FCSTD DOCUMENT  (FreeCAD 1.0R39319 (Git))
Label: 00_assembly_basic_grate
License: All rights reserved
LicenseURL: http://en.wikipedia.org/wiki/All_rights_reserved
objects: App::Link×27, App::FeaturePython×14, Assembly::AssemblyLink×7, TechDraw::DrawProjGroupItem×6, TechDraw::DrawViewBalloon×5, TechDraw::DrawProjGroup×2, TechDraw::DrawSVGTemplate×1, Assembly::JointGroup×1, Assembly::AssemblyObject×1, TechDraw::DrawViewAnnotation×1, TechDraw::DrawPage×1
EXTERNAL_REF file=01_assembly_frame.FCStd obj=Assembly
EXTERNAL_REF file=01_assembly_frame.FCStd obj=Body
EXTERNAL_REF file=01_assembly_frame.FCStd obj=Body001
EXTERNAL_REF file=01_assembly_frame.FCStd obj=Body002
EXTERNAL_REF file=01_assembly_frame.FCStd obj=Body003
EXTERNAL_REF file=01_assembly_frame.FCStd obj=Body004
EXTERNAL_REF file=01_assembly_frame.FCStd obj=Body005
EXTERNAL_REF file=01_assembly_frame.FCStd obj=Body006
EXTERNAL_REF file=10_assembly_lamella_no_knob.FCStd obj=Assembly
EXTERNAL_REF file=10_assembly_lamella_no_knob.FCStd obj=Body
EXTERNAL_REF file=10_assembly_lamella_no_knob.FCStd obj=Body001
EXTERNAL_REF file=10_assembly_lamella_no_knob.FCStd obj=Body002
EXTERNAL_REF file=11_assembly_lamella_knob.FCStd obj=Assembly
EXTERNAL_REF file=11_assembly_lamella_knob.FCStd obj=Body
EXTERNAL_REF file=11_assembly_lamella_knob.FCStd obj=Body001
EXTERNAL_REF file=11_assembly_lamella_knob.FCStd obj=Body002
EXTERNAL_REF file=11_assembly_lamella_knob.FCStd obj=Body003
EXTERNAL_REF file=05_lamella_mechanic_beam.FCStd obj=Body

FEATURE [App::Link] Body
  LinkedObject = -> <external 01_assembly_frame.FCStd>#Body
FEATURE [App::Link] Body001
  LinkPlacement = pos=(230,-210,15) rot=(1,0,0;1.5708rad)
  LinkedObject = -> <external 01_assembly_frame.FCStd>#Body001
  Placement = pos=(230,-210,15) rot=(1,0,0;1.5708rad)
FEATURE [App::Link] Body002
  LinkPlacement = pos=(138,-210,15) rot=(1,0,0;1.5708rad)
  LinkedObject = -> <external 01_assembly_frame.FCStd>#Body002
  Placement = pos=(138,-210,15) rot=(1,0,0;1.5708rad)
FEATURE [App::Link] Body003
  LinkPlacement = pos=(46,-210,15) rot=(1,0,0;1.5708rad)
  LinkedObject = -> <external 01_assembly_frame.FCStd>#Body003
  Placement = pos=(46,-210,15) rot=(1,0,0;1.5708rad)
FEATURE [App::Link] Body004
  LinkPlacement = pos=(-46,-210,15) rot=(1,0,0;1.5708rad)
  LinkedObject = -> <external 01_assembly_frame.FCStd>#Body004
  Placement = pos=(-46,-210,15) rot=(1,0,0;1.5708rad)
FEATURE [App::Link] Body005
  LinkPlacement = pos=(-138,-210,15) rot=(1,0,0;1.5708rad)
  LinkedObject = -> <external 01_assembly_frame.FCStd>#Body005
  Placement = pos=(-138,-210,15) rot=(1,0,0;1.5708rad)
FEATURE [App::Link] Body006
  LinkPlacement = pos=(-230,-210,15) rot=(1,0,0;1.5708rad)
  LinkedObject = -> <external 01_assembly_frame.FCStd>#Body006
  Placement = pos=(-230,-210,15) rot=(1,0,0;1.5708rad)
FEATURE [Assembly::AssemblyLink] Assembly001
  Group = -> [Body,Body001,Body002,Body003,Body004,Body005,Body006]
  LinkedObject = -> <external 01_assembly_frame.FCStd>#Assembly
  Origin = -> Origin001
  Rigid = true
FEATURE [App::FeaturePython] GroundedJoint  # Assembly grounded joint (typed FeaturePython)
  ObjectToGround = -> Assembly001
FEATURE [App::Link] Body007
  LinkedObject = -> <external 10_assembly_lamella_no_knob.FCStd>#Body
FEATURE [App::Link] Body008
  LinkPlacement = pos=(-9.4e-15,-6e-15,4.5) rot=(0,0,1;0rad)
  LinkedObject = -> <external 10_assembly_lamella_no_knob.FCStd>#Body001
  Placement = pos=(-9.4e-15,-6e-15,4.5) rot=(0,0,1;0rad)
FEATURE [App::Link] Body009
  LinkPlacement = pos=(-4,77.5,1.5) rot=(0,-1,0;1.5708rad)
  LinkedObject = -> <external 10_assembly_lamella_no_knob.FCStd>#Body002
  Placement = pos=(-4,77.5,1.5) rot=(0,-1,0;1.5708rad)
FEATURE [Assembly::AssemblyLink] Assembly002
  Group = -> [Body007,Body008,Body009]
  LinkedObject = -> <external 10_assembly_lamella_no_knob.FCStd>#Assembly
  Origin = -> Origin002
  Placement = pos=(-231.939,-1.29e-14,19.0609) rot=(0.698211,-0.698211,0.158123;3.45524rad)
  Rigid = true
FEATURE [App::Link] Body010
  LinkedObject = -> <external 10_assembly_lamella_no_knob.FCStd>#Body
FEATURE [App::Link] Body011
  LinkPlacement = pos=(-9.4e-15,-6e-15,4.5) rot=(0,0,1;0rad)
  LinkedObject = -> <external 10_assembly_lamella_no_knob.FCStd>#Body001
  Placement = pos=(-9.4e-15,-6e-15,4.5) rot=(0,0,1;0rad)
FEATURE [App::Link] Body012
  LinkPlacement = pos=(-4,77.5,1.5) rot=(0,-1,0;1.5708rad)
  LinkedObject = -> <external 10_assembly_lamella_no_knob.FCStd>#Body002
  Placement = pos=(-4,77.5,1.5) rot=(0,-1,0;1.5708rad)
FEATURE [Assembly::AssemblyLink] Assembly003
  Group = -> [Body010,Body011,Body012]
  LinkedObject = -> <external 10_assembly_lamella_no_knob.FCStd>#Assembly
  Origin = -> Origin003
  Placement = pos=(136.061,-1.49e-14,19.0609) rot=(-0.698211,0.698211,-0.158123;2.82794rad)
  Rigid = true
FEATURE [App::Link] Body013
  LinkedObject = -> <external 11_assembly_lamella_knob.FCStd>#Body
FEATURE [App::Link] Body014
  LinkPlacement = pos=(-1.1e-14,-5.1e-15,4.5) rot=(1,0,0;3.14159rad)
  LinkedObject = -> <external 11_assembly_lamella_knob.FCStd>#Body001
  Placement = pos=(-1.1e-14,-5.1e-15,4.5) rot=(1,0,0;3.14159rad)
FEATURE [App::Link] Body015
  LinkPlacement = pos=(-5,77.5,1.5) rot=(0,-1,0;1.5708rad)
  LinkedObject = -> <external 11_assembly_lamella_knob.FCStd>#Body002
  Placement = pos=(-5,77.5,1.5) rot=(0,-1,0;1.5708rad)
FEATURE [App::Link] Body016
  LinkPlacement = pos=(8,-30,-1.5) rot=(0.57735,0.57735,-0.57735;2.0944rad)
  LinkedObject = -> <external 11_assembly_lamella_knob.FCStd>#Body003
  Placement = pos=(8,-30,-1.5) rot=(0.57735,0.57735,-0.57735;2.0944rad)
FEATURE [Assembly::AssemblyLink] Assembly004
  Group = -> [Body013,Body014,Body015,Body016]
  LinkedObject = -> <external 11_assembly_lamella_knob.FCStd>#Assembly
  Origin = -> Origin004
  Placement = pos=(-47.9388,4.1e-15,19.0609) rot=(0.698211,-0.698211,0.158123;3.45524rad)
  Rigid = true
FEATURE [App::Link] Body017
  LinkedObject = -> <external 10_assembly_lamella_no_knob.FCStd>#Body
FEATURE [App::Link] Body018
  LinkPlacement = pos=(-9.4e-15,-6e-15,4.5) rot=(0,0,1;0rad)
  LinkedObject = -> <external 10_assembly_lamella_no_knob.FCStd>#Body001
  Placement = pos=(-9.4e-15,-6e-15,4.5) rot=(0,0,1;0rad)
FEATURE [App::Link] Body019
  LinkPlacement = pos=(-4,77.5,1.5) rot=(0,-1,0;1.5708rad)
  LinkedObject = -> <external 10_assembly_lamella_no_knob.FCStd>#Body002
  Placement = pos=(-4,77.5,1.5) rot=(0,-1,0;1.5708rad)
FEATURE [Assembly::AssemblyLink] Assembly005
  Group = -> [Body017,Body018,Body019]
  LinkedObject = -> <external 10_assembly_lamella_no_knob.FCStd>#Assembly
  Origin = -> Origin005
  Placement = pos=(44.0612,1.07e-14,19.0609) rot=(-0.698211,0.698211,-0.158123;2.82794rad)
  Rigid = true
FEATURE [App::Link] Body020
  LinkedObject = -> <external 10_assembly_lamella_no_knob.FCStd>#Body
FEATURE [App::Link] Body021
  LinkPlacement = pos=(-9.4e-15,-6e-15,4.5) rot=(0,0,1;0rad)
  LinkedObject = -> <external 10_assembly_lamella_no_knob.FCStd>#Body001
  Placement = pos=(-9.4e-15,-6e-15,4.5) rot=(0,0,1;0rad)
FEATURE [App::Link] Body022
  LinkPlacement = pos=(-4,77.5,1.5) rot=(0,-1,0;1.5708rad)
  LinkedObject = -> <external 10_assembly_lamella_no_knob.FCStd>#Body002
  Placement = pos=(-4,77.5,1.5) rot=(0,-1,0;1.5708rad)
FEATURE [Assembly::AssemblyLink] Assembly006
  Group = -> [Body020,Body021,Body022]
  LinkedObject = -> <external 10_assembly_lamella_no_knob.FCStd>#Assembly
  Origin = -> Origin006
  Placement = pos=(-139.939,5.42e-14,19.0609) rot=(0.698211,-0.698211,0.158123;3.45524rad)
  Rigid = true
FEATURE [App::Link] Body023
  LinkedObject = -> <external 10_assembly_lamella_no_knob.FCStd>#Body
FEATURE [App::Link] Body024
  LinkPlacement = pos=(-9.4e-15,-6e-15,4.5) rot=(0,0,1;0rad)
  LinkedObject = -> <external 10_assembly_lamella_no_knob.FCStd>#Body001
  Placement = pos=(-9.4e-15,-6e-15,4.5) rot=(0,0,1;0rad)
FEATURE [App::Link] Body025
  LinkPlacement = pos=(-4,77.5,1.5) rot=(0,-1,0;1.5708rad)
  LinkedObject = -> <external 10_assembly_lamella_no_knob.FCStd>#Body002
  Placement = pos=(-4,77.5,1.5) rot=(0,-1,0;1.5708rad)
FEATURE [Assembly::AssemblyLink] Assembly007
  Group = -> [Body023,Body024,Body025]
  LinkedObject = -> <external 10_assembly_lamella_no_knob.FCStd>#Assembly
  Origin = -> Origin007
  Placement = pos=(228.061,2.14e-14,19.0609) rot=(-0.698211,0.698211,-0.158123;2.82794rad)
  Rigid = true
FEATURE [App::Link] Body026
  LinkPlacement = pos=(-51.2317,6.5,-22.7566) rot=(0.57735,0.57735,0.57735;4.18879rad)
  LinkedObject = -> <external 05_lamella_mechanic_beam.FCStd>#Body
  Placement = pos=(-51.2317,6.5,-22.7566) rot=(0.57735,0.57735,0.57735;4.18879rad)
FEATURE [TechDraw::DrawSVGTemplate] Template
  EditableTexts = AuthorName=Matthias Mosimann; CheckDate=N/A; CreationDate=15/04/2026; DrawingNumber=1.0; FC-Title=Kellerfenster; SheetNumber=1 / 1; SupervisorName=N/A; Weight=N/A; scale=1 : 5
  Height = 297
  Orientation = 1
  Template = C:/Program Files/FreeCAD 1.0/data/Mod/TechDraw/Templates/A3_Landscape_TD.svg
  Width = 420
FEATURE [App::FeaturePython] Joint  label="REVL1"  # Assembly joint (typed FeaturePython)
  Activated = true
  AngleMax = 0
  AngleMin = 0
  Detach1 = false
  Detach2 = false
  Distance = 0
  Distance2 = 0
  EnableAngleMax = false
  EnableAngleMin = false
  EnableLengthMax = false
  EnableLengthMin = false
  JointType = 1 (Revolute)
  LengthMax = 0
  LengthMin = 0
  Offset2 = pos=(0,0,7) rot=(0,0,1;0rad)
  Placement1 = pos=(217,0,0) rot=(0.57735,0.57735,0.57735;2.0944rad)
  Placement2 = pos=(0,0,7) rot=(0,0,1;0rad)
  Reference1 = -> Assembly [Assembly002.Body008.Edge18,Assembly002.Body008.Edge18]
  Reference2 = -> Assembly [Assembly001.Body006.Edge4,Assembly001.Body006.Edge4]
FEATURE [App::FeaturePython] Joint001  label="REVL2"  # Assembly joint (typed FeaturePython)
  Activated = true
  AngleMax = 0
  AngleMin = 0
  Detach1 = false
  Detach2 = false
  Distance = 0
  Distance2 = 0
  EnableAngleMax = false
  EnableAngleMin = false
  EnableLengthMax = false
  EnableLengthMin = false
  JointType = 1 (Revolute)
  LengthMax = 0
  LengthMin = 0
  Offset2 = pos=(0,0,7) rot=(0,0,1;0rad)
  Placement1 = pos=(217,0,0) rot=(0.57735,0.57735,0.57735;2.0944rad)
  Placement2 = pos=(0,0,7) rot=(0,0,1;0rad)
  Reference1 = -> Assembly [Assembly006.Body021.Edge18,Assembly006.Body021.Edge18]
  Reference2 = -> Assembly [Assembly001.Body005.Edge4,Assembly001.Body005.Edge4]
FEATURE [App::FeaturePython] Joint002  label="REVL3"  # Assembly joint (typed FeaturePython)
  Activated = true
  AngleMax = 0
  AngleMin = 0
  Detach1 = false
  Detach2 = false
  Distance = 0
  Distance2 = 0
  EnableAngleMax = false
  EnableAngleMin = false
  EnableLengthMax = false
  EnableLengthMin = false
  JointType = 1 (Revolute)
  LengthMax = 0
  LengthMin = 0
  Offset2 = pos=(0,0,7) rot=(0,0,1;0rad)
  Placement1 = pos=(217,0,0) rot=(0.57735,0.57735,0.57735;2.0944rad)
  Placement2 = pos=(0,0,7) rot=(0,0,1;0rad)
  Reference1 = -> Assembly [Assembly004.Body014.Edge18,Assembly004.Body014.Edge18]
  Reference2 = -> Assembly [Assembly001.Body004.Edge4,Assembly001.Body004.Edge4]
FEATURE [App::FeaturePython] Joint003  label="Revolute"  # Assembly joint (typed FeaturePython)
  Activated = true
  AngleMax = 0
  AngleMin = 0
  Detach1 = false
  Detach2 = false
  Distance = 0
  Distance2 = 0
  EnableAngleMax = false
  EnableAngleMin = false
  EnableLengthMax = false
  EnableLengthMin = false
  JointType = 1 (Revolute)
  LengthMax = 0
  LengthMin = 0
  Placement1 = pos=(-2.84e-14,-230,-2.5) rot=(0,0,1;0rad)
  Placement2 = pos=(15,-15,-4e-16) rot=(0,0,1;0rad)
  Reference1 = -> Assembly [Body026.Edge44,Body026.Edge44]
  Reference2 = -> Assembly [Assembly002.Body009.Edge7,Assembly002.Body009.Edge7]
FEATURE [App::FeaturePython] Joint004  label="Parallel"  # Assembly joint (typed FeaturePython)
  Activated = true
  AngleMax = 0
  AngleMin = 0
  Detach1 = false
  Detach2 = false
  Distance = 0
  Distance2 = 0
  EnableAngleMax = false
  EnableAngleMin = false
  EnableLengthMax = false
  EnableLengthMin = false
  JointType = 6 (Parallel)
  LengthMax = 0
  LengthMin = 0
  Placement1 = pos=(-208,-50,-1.5) rot=(0,0,1;0rad)
  Placement2 = pos=(1e-15,3e-16,-1.5) rot=(0,0,1;0rad)
  Reference1 = -> Assembly [Assembly002.Body007.Face5,Assembly002.Body007.Vertex3]
  Reference2 = -> Assembly [Assembly006.Body020.Face5,Assembly006.Body020.Face5]
FEATURE [App::FeaturePython] Joint005  label="Revolute001"  # Assembly joint (typed FeaturePython)
  Activated = true
  AngleMax = 0
  AngleMin = 0
  Detach1 = false
  Detach2 = false
  Distance = 0
  Distance2 = 0
  EnableAngleMax = false
  EnableAngleMin = false
  EnableLengthMax = false
  EnableLengthMin = false
  JointType = 1 (Revolute)
  LengthMax = 0
  LengthMin = 0
  Placement1 = pos=(-1.78e-14,-138,-2.5) rot=(0,0,1;0rad)
  Placement2 = pos=(15,-15,-4e-16) rot=(0,0,1;0rad)
  Reference1 = -> Assembly [Body026.Edge45,Body026.Edge45]
  Reference2 = -> Assembly [Assembly006.Body022.Edge7,Assembly006.Body022.Edge7]
FEATURE [App::FeaturePython] Joint006  label="Parallel001"  # Assembly joint (typed FeaturePython)
  Activated = true
  AngleMax = 0
  AngleMin = 0
  Detach1 = false
  Detach2 = false
  Distance = 0
  Distance2 = 0
  EnableAngleMax = false
  EnableAngleMin = false
  EnableLengthMax = false
  EnableLengthMin = false
  JointType = 6 (Parallel)
  LengthMax = 0
  LengthMin = 0
  Placement1 = pos=(1e-15,3e-16,-1.5) rot=(0,0,1;0rad)
  Placement2 = pos=(-0.00619131,0.0232174,-1.5) rot=(0,0,1;0rad)
  Reference1 = -> Assembly [Assembly002.Body007.Face5,Assembly002.Body007.Face5]
  Reference2 = -> Assembly [Assembly004.Body013.Face8,Assembly004.Body013.Face8]
FEATURE [App::FeaturePython] Joint007  label="Revolute002"  # Assembly joint (typed FeaturePython)
  Activated = true
  AngleMax = 0
  AngleMin = 0
  Detach1 = false
  Detach2 = false
  Distance = 0
  Distance2 = 0
  EnableAngleMax = false
  EnableAngleMin = false
  EnableLengthMax = false
  EnableLengthMin = false
  JointType = 1 (Revolute)
  LengthMax = 0
  LengthMin = 0
  Offset2 = pos=(0,0,7) rot=(0,0,1;0rad)
  Placement1 = pos=(217,0,0) rot=(0.57735,0.57735,0.57735;2.0944rad)
  Placement2 = pos=(0,0,7) rot=(0,0,1;0rad)
  Reference1 = -> Assembly [Assembly005.Body018.Edge18,Assembly005.Body018.Edge18]
  Reference2 = -> Assembly [Assembly001.Body003.Edge4,Assembly001.Body003.Edge4]
FEATURE [App::FeaturePython] Joint008  label="Parallel002"  # Assembly joint (typed FeaturePython)
  Activated = true
  AngleMax = 0
  AngleMin = 0
  Detach1 = false
  Detach2 = false
  Distance = 0
  Distance2 = 0
  EnableAngleMax = false
  EnableAngleMin = false
  EnableLengthMax = false
  EnableLengthMin = false
  JointType = 6 (Parallel)
  LengthMax = 0
  LengthMin = 0
  Placement1 = pos=(1e-15,3e-16,-1.5) rot=(0,0,1;0rad)
  Placement2 = pos=(1e-15,3e-16,-1.5) rot=(0,0,1;0rad)
  Reference1 = -> Assembly [Assembly002.Body007.Face5,Assembly002.Body007.Face5]
  Reference2 = -> Assembly [Assembly005.Body017.Face5,Assembly005.Body017.Face5]
FEATURE [App::FeaturePython] Joint009  label="Revolute003"  # Assembly joint (typed FeaturePython)
  Activated = true
  AngleMax = 0
  AngleMin = 0
  Detach1 = false
  Detach2 = false
  Distance = 0
  Distance2 = 0
  EnableAngleMax = false
  EnableAngleMin = false
  EnableLengthMax = false
  EnableLengthMin = false
  JointType = 1 (Revolute)
  LengthMax = 0
  LengthMin = 0
  Offset2 = pos=(0,0,7) rot=(0,0,1;0rad)
  Placement1 = pos=(217,0,0) rot=(0.57735,0.57735,0.57735;2.0944rad)
  Placement2 = pos=(0,0,7) rot=(0,0,1;0rad)
  Reference1 = -> Assembly [Assembly003.Body011.Edge18,Assembly003.Body011.Edge18]
  Reference2 = -> Assembly [Assembly001.Body002.Edge4,Assembly001.Body002.Edge4]
FEATURE [App::FeaturePython] Joint010  label="Parallel003"  # Assembly joint (typed FeaturePython)
  Activated = true
  AngleMax = 0
  AngleMin = 0
  Detach1 = false
  Detach2 = false
  Distance = 0
  Distance2 = 0
  EnableAngleMax = false
  EnableAngleMin = false
  EnableLengthMax = false
  EnableLengthMin = false
  JointType = 6 (Parallel)
  LengthMax = 0
  LengthMin = 0
  Placement1 = pos=(1e-15,3e-16,-1.5) rot=(0,0,1;0rad)
  Placement2 = pos=(1e-15,3e-16,-1.5) rot=(0,0,1;0rad)
  Reference1 = -> Assembly [Assembly002.Body007.Face5,Assembly002.Body007.Face5]
  Reference2 = -> Assembly [Assembly003.Body010.Face5,Assembly003.Body010.Face5]
FEATURE [App::FeaturePython] Joint011  label="Revolute004"  # Assembly joint (typed FeaturePython)
  Activated = true
  AngleMax = 0
  AngleMin = 0
  Detach1 = false
  Detach2 = false
  Distance = 0
  Distance2 = 0
  EnableAngleMax = false
  EnableAngleMin = false
  EnableLengthMax = false
  EnableLengthMin = false
  JointType = 1 (Revolute)
  LengthMax = 0
  LengthMin = 0
  Offset2 = pos=(0,0,7) rot=(0,0,1;0rad)
  Placement1 = pos=(217,0,0) rot=(0.57735,0.57735,0.57735;2.0944rad)
  Placement2 = pos=(0,0,7) rot=(0,0,1;0rad)
  Reference1 = -> Assembly [Assembly007.Body024.Edge18,Assembly007.Body024.Edge18]
  Reference2 = -> Assembly [Assembly001.Body001.Edge4,Assembly001.Body001.Edge4]
FEATURE [App::FeaturePython] Joint012  label="Parallel004"  # Assembly joint (typed FeaturePython)
  Activated = true
  AngleMax = 0
  AngleMin = 0
  Detach1 = false
  Detach2 = false
  Distance = 0
  Distance2 = 0
  EnableAngleMax = false
  EnableAngleMin = false
  EnableLengthMax = false
  EnableLengthMin = false
  JointType = 6 (Parallel)
  LengthMax = 0
  LengthMin = 0
  Placement1 = pos=(1e-15,3e-16,-1.5) rot=(0,0,1;0rad)
  Placement2 = pos=(1e-15,3e-16,-1.5) rot=(0,0,1;0rad)
  Reference1 = -> Assembly [Assembly002.Body007.Face5,Assembly002.Body007.Face5]
  Reference2 = -> Assembly [Assembly007.Body023.Face5,Assembly007.Body023.Face5]
FEATURE [Assembly::JointGroup] Joints
  Group = -> [GroundedJoint,Joint,Joint001,Joint002,Joint003,Joint004,Joint005,Joint006,Joint007,Joint008,Joint009,Joint010,Joint011,Joint012]
FEATURE [Assembly::AssemblyObject] Assembly
  Group = -> [Joints,Assembly001,GroundedJoint,Assembly002,Assembly003,Assembly004,Assembly005,Assembly006,Assembly007,Body026,Joint,Joint001,Joint002,Joint003,Joint004,Joint005,Joint006,Joint007,Joint008,Joint009,Joint010,Joint011,Joint012]
  Origin = -> Origin
  Type = Assembly
FEATURE [TechDraw::DrawProjGroupItem] View  label="Front"
  CoarseView = false
  Direction = (0,-1,0)
  Focus = 100
  HardHidden = false
  IsoCount = 0
  IsoHidden = false
  IsoVisible = false
  LockPosition = true
  Perspective = false
  Rotation = 0
  RotationVector = (1,0,0)
  Scale = 0.166667
  ScaleType = 2
  ScrubCount = 1
  SeamHidden = false
  SeamVisible = true
  SmoothHidden = false
  SmoothVisible = true
  Source = -> [Assembly]
  Type = 0
  X = 0
  XDirection = (1,0,2e-16)
  Y = 0
FEATURE [TechDraw::DrawProjGroupItem] ProjItem  label="Bottom"
  CoarseView = false
  Direction = (2e-16,0,-1)
  Focus = 100
  HardHidden = false
  IsoCount = 0
  IsoHidden = false
  IsoVisible = false
  LockPosition = false
  Perspective = false
  Rotation = 0
  RotationVector = (1,0,0)
  Scale = 0.166667
  ScaleType = 0
  ScrubCount = 1
  SeamHidden = false
  SeamVisible = true
  SmoothHidden = false
  SmoothVisible = true
  Source = -> [Assembly]
  Type = 5
  X = 0
  XDirection = (1,0,2e-16)
  Y = 61.1435
FEATURE [TechDraw::DrawProjGroupItem] ProjItem001  label="Top"
  CoarseView = false
  Direction = (-2e-16,0,1)
  Focus = 100
  HardHidden = true
  IsoCount = 0
  IsoHidden = false
  IsoVisible = false
  LockPosition = false
  Perspective = false
  Rotation = 0
  RotationVector = (1,0,0)
  Scale = 0.166667
  ScaleType = 0
  ScrubCount = 1
  SeamHidden = false
  SeamVisible = true
  SmoothHidden = false
  SmoothVisible = true
  Source = -> [Assembly]
  Type = 4
  X = 0
  XDirection = (1,0,2e-16)
  Y = -61.1435
FEATURE [TechDraw::DrawProjGroupItem] ProjItem002  label="Left"
  CoarseView = false
  Direction = (-1,-1e-16,-2e-16)
  Focus = 100
  HardHidden = false
  IsoCount = 0
  IsoHidden = false
  IsoVisible = false
  LockPosition = false
  Perspective = false
  Rotation = 0
  RotationVector = (1,0,0)
  Scale = 0.166667
  ScaleType = 0
  ScrubCount = 1
  SeamHidden = false
  SeamVisible = true
  SmoothHidden = false
  SmoothVisible = true
  Source = -> [Assembly]
  Type = 1
  X = 102.353
  XDirection = (1e-16,-1,0)
  Y = 0
FEATURE [TechDraw::DrawProjGroupItem] ProjItem003  label="Right"
  CoarseView = false
  Direction = (1,-1e-16,2e-16)
  Focus = 100
  HardHidden = false
  IsoCount = 0
  IsoHidden = false
  IsoVisible = false
  LockPosition = false
  Perspective = false
  Rotation = 0
  RotationVector = (1,0,0)
  Scale = 0.166667
  ScaleType = 0
  ScrubCount = 1
  SeamHidden = false
  SeamVisible = true
  SmoothHidden = false
  SmoothVisible = true
  Source = -> [Assembly]
  Type = 2
  X = -102.353
  XDirection = (1e-16,1,0)
  Y = 0
FEATURE [TechDraw::DrawProjGroup] ProjGroup
  Anchor = -> View
  AutoDistribute = true
  LockPosition = false
  ProjectionType = 0
  Rotation = 0
  Scale = 0.166667
  ScaleType = 2
  Source = -> [Assembly]
  Views = -> [View,ProjItem,ProjItem001,ProjItem002,ProjItem003]
  X = 157.599
  Y = 178.244
  spacingX = 15
  spacingY = 15
FEATURE [TechDraw::DrawProjGroupItem] View001  label="Front001"
  CoarseView = false
  Direction = (0.57735,0.57735,0.57735)
  Focus = 100
  HardHidden = false
  IsoCount = 0
  IsoHidden = false
  IsoVisible = false
  LockPosition = true
  Perspective = false
  Rotation = 0
  RotationVector = (0.707107,0,-0.707107)
  Scale = 0.166667
  ScaleType = 2
  ScrubCount = 1
  SeamHidden = false
  SeamVisible = true
  SmoothHidden = false
  SmoothVisible = true
  Source = -> [Assembly]
  Type = 0
  X = 0
  XDirection = (0.707107,0,-0.707107)
  Y = 0
FEATURE [TechDraw::DrawProjGroup] ProjGroup001
  Anchor = -> View001
  AutoDistribute = true
  LockPosition = false
  ProjectionType = 0
  Rotation = 0
  Scale = 0.166667
  ScaleType = 2
  Source = -> [Assembly]
  Views = -> [View001]
  X = 363.678
  Y = 132.846
  spacingX = 15
  spacingY = 15
FEATURE [TechDraw::DrawViewAnnotation] Annotation
  Font = osifont
  LineSpace = 80
  LockPosition = false
  MaxWidth = 140
  Rotation = 0
  Scale = 0.5
  ScaleType = 1
  Text = (1) Lamelle 3 von links hat den Griff. Unbedingt einhalten! | (2) Ausschnitt ist links im Rahmen. Unbedingt einhalten! (Mauer Aussparung vorhanden) | (3) Edelstahlhülsen sind unten | (4) 1mm Luft einkalkuliert in 4.1mm Sackloch | (5) Lamellen haben im Moment unten und oben 2mm Luft einkalkuliert.
  TextSize = 3
  TextStyle = 0
  X = 81.1672
  Y = 39.4162
FEATURE [TechDraw::DrawViewBalloon] Balloon
  BubbleShape = 0
  EndType = 0
  EndTypeScale = 1
  KinkLength = 5
  LockPosition = false
  OriginX = -54.8567
  OriginY = 100.049
  Rotation = 0
  ScaleType = 0
  ShapeScale = 1
  SourceView = -> View001
  Text = 1
  TextWrapLen = -1
  X = 65.1431
  Y = 220.048
FEATURE [TechDraw::DrawViewBalloon] Balloon002
  BubbleShape = 0
  EndType = 0
  EndTypeScale = 1
  KinkLength = 5
  LockPosition = false
  OriginX = -232.885
  OriginY = -217.5
  Rotation = 0
  ScaleType = 0
  ShapeScale = 1
  SourceView = -> ProjItem001
  Text = 3
  TextWrapLen = -1
  X = -355.161
  Y = -284.214
FEATURE [TechDraw::DrawViewBalloon] Balloon003
  BubbleShape = 0
  EndType = 0
  EndTypeScale = 1
  KinkLength = 5
  LockPosition = false
  OriginX = -229.935
  OriginY = 214
  Rotation = 0
  ScaleType = 0
  ShapeScale = 1
  SourceView = -> ProjItem001
  Text = 4
  TextWrapLen = -1
  X = -374.485
  Y = 276.903
FEATURE [TechDraw::DrawViewBalloon] Balloon004
  BubbleShape = 0
  EndType = 0
  EndTypeScale = 1
  KinkLength = 5
  LockPosition = false
  OriginX = -197.99
  OriginY = 115.943
  Rotation = 0
  ScaleType = 0
  ShapeScale = 1
  SourceView = -> View001
  Text = 3
  TextWrapLen = -1
  X = -329.578
  Y = 24.8785
FEATURE [TechDraw::DrawViewBalloon] Balloon005
  BubbleShape = 0
  EndType = 0
  EndTypeScale = 1
  KinkLength = 5
  LockPosition = false
  OriginX = -229.177
  OriginY = 208
  Rotation = 0
  ScaleType = 0
  ShapeScale = 1
  SourceView = -> ProjItem001
  Text = 5
  TextWrapLen = -1
  X = -422.216
  Y = 111.151
FEATURE [TechDraw::DrawPage] Page
  KeepUpdated = true
  NextBalloonIndex = 7
  ProjectionType = 0
  Template = -> Template
  Views = -> [ProjGroup,ProjGroup001,Annotation,Balloon,Balloon002,Balloon003,Balloon004,Balloon005]

RESOLVED EXTERNAL PARTS (link-assembly join: the EXTERNAL_REF files above that resolve inside this repo's crawl, each included once):
---- part 01_assembly_frame.FCStd = doc fcstd_7cfaef1b82c4 ----
FCSTD DOCUMENT  (FreeCAD 1.0R39319 (Git))
Label: 01_assembly_frame
License: All rights reserved
LicenseURL: http://en.wikipedia.org/wiki/All_rights_reserved
objects: App::Link×7, App::FeaturePython×7, Assembly::JointGroup×1, Assembly::AssemblyObject×1
EXTERNAL_REF file=02_frame_15_x_30.FCStd obj=Body
EXTERNAL_REF file=03_frame_sleeve.FCStd obj=Body

FEATURE [App::Link] Body
  LinkedObject = -> <external 02_frame_15_x_30.FCStd>#Body
FEATURE [App::FeaturePython] GroundedJoint  # Assembly grounded joint (typed FeaturePython)
  ObjectToGround = -> Body
FEATURE [App::Link] Body001
  LinkPlacement = pos=(230,-210,15) rot=(1,0,0;1.5708rad)
  LinkedObject = -> <external 03_frame_sleeve.FCStd>#Body
  Placement = pos=(230,-210,15) rot=(1,0,0;1.5708rad)
FEATURE [App::Link] Body002
  LinkPlacement = pos=(138,-210,15) rot=(1,0,0;1.5708rad)
  LinkedObject = -> <external 03_frame_sleeve.FCStd>#Body
  Placement = pos=(138,-210,15) rot=(1,0,0;1.5708rad)
FEATURE [App::Link] Body003
  LinkPlacement = pos=(46,-210,15) rot=(1,0,0;1.5708rad)
  LinkedObject = -> <external 03_frame_sleeve.FCStd>#Body
  Placement = pos=(46,-210,15) rot=(1,0,0;1.5708rad)
FEATURE [App::Link] Body004
  LinkPlacement = pos=(-46,-210,15) rot=(1,0,0;1.5708rad)
  LinkedObject = -> <external 03_frame_sleeve.FCStd>#Body
  Placement = pos=(-46,-210,15) rot=(1,0,0;1.5708rad)
FEATURE [App::Link] Body005
  LinkPlacement = pos=(-138,-210,15) rot=(1,0,0;1.5708rad)
  LinkedObject = -> <external 03_frame_sleeve.FCStd>#Body
  Placement = pos=(-138,-210,15) rot=(1,0,0;1.5708rad)
FEATURE [App::Link] Body006
  LinkPlacement = pos=(-230,-210,15) rot=(1,0,0;1.5708rad)
  LinkedObject = -> <external 03_frame_sleeve.FCStd>#Body
  Placement = pos=(-230,-210,15) rot=(1,0,0;1.5708rad)
FEATURE [App::FeaturePython] Joint  label="Revolute"  # Assembly joint (typed FeaturePython)
  Activated = true
  AngleMax = 0
  AngleMin = 0
  Detach1 = false
  Detach2 = false
  Distance = 0
  Distance2 = 0
  EnableAngleMax = false
  EnableAngleMin = false
  EnableLengthMax = false
  EnableLengthMin = false
  JointType = 1 (Revolute)
  LengthMax = 0
  LengthMin = 0
  Placement1 = pos=(0,0,15) rot=(0,0,1;0rad)
  Placement2 = pos=(0,-225,0) rot=(0.707107,0,0.707107;3.14159rad)
  Reference1 = -> Assembly [Body006.Edge3,Body006.Edge3]
  Reference2 = -> Assembly [Body.Edge26,Body.Edge26]
FEATURE [App::FeaturePython] Joint001  label="Revolute001"  # Assembly joint (typed FeaturePython)
  Activated = true
  AngleMax = 0
  AngleMin = 0
  Detach1 = false
  Detach2 = false
  Distance = 0
  Distance2 = 0
  EnableAngleMax = false
  EnableAngleMin = false
  EnableLengthMax = false
  EnableLengthMin = false
  JointType = 1 (Revolute)
  LengthMax = 0
  LengthMin = 0
  Placement1 = pos=(0,0,15) rot=(0,0,1;0rad)
  Placement2 = pos=(-289.5,-15,0) rot=(-0.707107,0,0.707107;3.14159rad)
  Reference1 = -> Assembly [Body005.Edge3,Body005.Edge3]
  Reference2 = -> Assembly [Body.Edge27,Body.Edge27]
FEATURE [App::FeaturePython] Joint002  label="Revolute002"  # Assembly joint (typed FeaturePython)
  Activated = true
  AngleMax = 0
  AngleMin = 0
  Detach1 = false
  Detach2 = false
  Distance = 0
  Distance2 = 0
  EnableAngleMax = false
  EnableAngleMin = false
  EnableLengthMax = false
  EnableLengthMin = false
  JointType = 1 (Revolute)
  LengthMax = 0
  LengthMin = 0
  Placement1 = pos=(0,0,15) rot=(0,0,1;0rad)
  Placement2 = pos=(0,-210,0) rot=(0.707107,0,0.707107;3.14159rad)
  Reference1 = -> Assembly [Body004.Edge3,Body004.Edge3]
  Reference2 = -> Assembly [Body.Edge28,Body.Edge28]
FEATURE [App::FeaturePython] Joint003  label="Revolute003"  # Assembly joint (typed FeaturePython)
  Activated = true
  AngleMax = 0
  AngleMin = 0
  Detach1 = false
  Detach2 = false
  Distance = 0
  Distance2 = 0
  EnableAngleMax = false
  EnableAngleMin = false
  EnableLengthMax = false
  EnableLengthMin = false
  JointType = 1 (Revolute)
  LengthMax = 0
  LengthMin = 0
  Placement1 = pos=(0,0,15) rot=(0,0,1;0rad)
  Placement2 = pos=(282,0,0) rot=(0.57735,0.57735,0.57735;4.18879rad)
  Reference1 = -> Assembly [Body003.Edge3,Body003.Edge3]
  Reference2 = -> Assembly [Body.Edge29,Body.Edge29]
FEATURE [App::FeaturePython] Joint004  label="Revolute004"  # Assembly joint (typed FeaturePython)
  Activated = true
  AngleMax = 0
  AngleMin = 0
  Detach1 = false
  Detach2 = false
  Distance = 0
  Distance2 = 0
  EnableAngleMax = false
  EnableAngleMin = false
  EnableLengthMax = false
  EnableLengthMin = false
  JointType = 1 (Revolute)
  LengthMax = 0
  LengthMin = 0
  Placement1 = pos=(0,0,15) rot=(0,0,1;0rad)
  Placement2 = pos=(0,210,0) rot=(-0.707107,0,0.707107;3.14159rad)
  Reference1 = -> Assembly [Body002.Edge3,Body002.Edge3]
  Reference2 = -> Assembly [Body.Edge30,Body.Edge30]
FEATURE [App::FeaturePython] Joint005  label="Revolute005"  # Assembly joint (typed FeaturePython)
  Activated = true
  AngleMax = 0
  AngleMin = 0
  Detach1 = false
  Detach2 = false
  Distance = 0
  Distance2 = 0
  EnableAngleMax = false
  EnableAngleMin = false
  EnableLengthMax = false
  EnableLengthMin = false
  JointType = 1 (Revolute)
  LengthMax = 0
  LengthMin = 0
  Placement1 = pos=(0,0,15) rot=(0,0,1;0rad)
  Placement2 = pos=(-289.5,15,0) rot=(-0.707107,0,0.707107;3.14159rad)
  Reference1 = -> Assembly [Body001.Edge3,Body001.Edge3]
  Reference2 = -> Assembly [Body.Edge31,Body.Edge31]
FEATURE [Assembly::JointGroup] Joints
  Group = -> [GroundedJoint,Joint,Joint001,Joint002,Joint003,Joint004,Joint005]
FEATURE [Assembly::AssemblyObject] Assembly
  Group = -> [Joints,Body,GroundedJoint,Body001,Body002,Body003,Body004,Body005,Body006,Joint,Joint001,Joint002,Joint003,Joint004,Joint005]
  Origin = -> Origin
  Type = Assembly
---- part 05_lamella_mechanic_beam.FCStd = doc fcstd_9dcb9582a534 ----
FCSTD DOCUMENT  (FreeCAD 1.0R39319 (Git))
Label: 05_lamella_mechanic_beam
License: All rights reserved
LicenseURL: http://en.wikipedia.org/wiki/All_rights_reserved
objects: TechDraw::DrawViewDimension×11, TechDraw::DrawProjGroupItem×5, Sketcher::SketchObject×2, TechDraw::DrawViewBalloon×2, TechDraw::DrawViewAnnotation×2, PartDesign::Pad×1, PartDesign::Pocket×1, PartDesign::Fillet×1, PartDesign::Chamfer×1, PartDesign::Body×1, TechDraw::DrawSVGTemplate×1, TechDraw::DrawProjGroup×1, TechDraw::DrawPage×1
note: 36 computed .brp shape members not serialized (recipe doc carries the construction recipe); baked Part::Feature solids carry a one-line shape summary decoded from their .brp

FEATURE [Sketcher::SketchObject] Sketch
  ArcFitTolerance = 1e-06
  AttachmentSupport = -> [XZ_Plane]
  FullyConstrained = true
  MakeInternals = false
  MapMode = 5
  Placement = pos=(0,0,0) rot=(1,0,0;1.5708rad)
  sketch-geometry (5):
    g0: LineSegment StartX=-10 StartY=2.5 StartZ=0 EndX=-10 EndY=-2.5 EndZ=0
    g1: LineSegment StartX=-10 StartY=-2.5 StartZ=0 EndX=10 EndY=-2.5 EndZ=0
    g2: LineSegment StartX=10 StartY=-2.5 StartZ=0 EndX=10 EndY=2.5 EndZ=0
    g3: LineSegment StartX=10 StartY=2.5 StartZ=0 EndX=-10 EndY=2.5 EndZ=0
    g4: LineSegment [constr] StartX=-10 StartY=2.5 StartZ=0 EndX=10 EndY=-2.5 EndZ=0
  constraints (13):
    c: Coincident(g0,g1)
    c: Coincident(g1,g2)
    c: Coincident(g2,g3)
    c: Coincident(g3,g0)
    c: Vertical(g0)
    c: Vertical(g2)
    c: Horizontal(g1)
    c: Horizontal(g3)
    c: Coincident(g4,g0)
    c: Coincident(g4,g1)
    c: Symmetric(g0,g1,g-1)
    c: Distance(g0,g0) = 5
    c: DistanceX(g3,g3) = 20
FEATURE [PartDesign::Pad] Pad
  Direction = (0,-1,2e-16)
  Length = 490
  Length2 = 10
  Midplane = true
  Placement = pos=(0,0,0) rot=(1,0,0;1.5708rad)
  Profile = -> Sketch
  ReferenceAxis = -> Sketch [N_Axis]
  Suppressed = false
  Type = 0
FEATURE [Sketcher::SketchObject] Sketch001
  ArcFitTolerance = 1e-06
  AttachmentSupport = -> [XY_Plane]
  ExternalGeometry = -> [Pad]
  FullyConstrained = true
  MakeInternals = false
  MapMode = 5
  sketch-geometry (7):
    g0: LineSegment [constr] StartX=-2.5e-15 StartY=245 StartZ=0 EndX=-1.3e-15 EndY=-245 EndZ=0
    g1: Circle CenterX=-1.3e-15 CenterY=-230 CenterZ=0 NormalX=0 NormalY=0 NormalZ=1 AngleXU=0 Radius=2.15
    g2: Circle CenterX=-1.6e-15 CenterY=-138 CenterZ=0 NormalX=0 NormalY=0 NormalZ=1 AngleXU=0 Radius=2.15
    g3: Circle CenterX=-1.8e-15 CenterY=-46 CenterZ=0 NormalX=0 NormalY=0 NormalZ=1 AngleXU=0 Radius=2.15
    g4: Circle CenterX=-2e-15 CenterY=46 CenterZ=0 NormalX=0 NormalY=0 NormalZ=1 AngleXU=0 Radius=2.15
    g5: Circle CenterX=-2.3e-15 CenterY=138 CenterZ=0 NormalX=0 NormalY=0 NormalZ=1 AngleXU=0 Radius=2.15
    g6: Circle CenterX=-2.5e-15 CenterY=230 CenterZ=0 NormalX=0 NormalY=0 NormalZ=1 AngleXU=0 Radius=2.15
  constraints (21):
    c: Symmetric(g-4,g-4,g0)
    c: Symmetric(g-3,g-3,g0)
    c: PointOnObject(g1,g0)
    c: Diameter(g1) = 4.3
    c: Distance(g0,g1) = 15
    c: PointOnObject(g2,g0)
    c: PointOnObject(g3,g0)
    c: Equal(g1,g2)
    c: Equal(g1,g3)
    c: DistanceY(g1,g2) = 92
    c: DistanceY(g2,g3) = 92
    c: PointOnObject(g4,g0)
    c: Equal(g1,g4)
    c: DistanceY(g3,g4) = 92
    c: PointOnObject(g5,g0)
    c: DistanceY(g4,g5) = 92
    c: Equal(g1,g5)
    c: PointOnObject(g6,g0)
    c: Equal(g1,g6)
    c: DistanceY(g5,g6) = 92
    c: Distance(g6,g0) = 15
FEATURE [PartDesign::Pocket] Pocket
  BaseFeature = -> Pad
  Direction = (0,0,-1)
  Length = 5
  Length2 = 5
  Midplane = true
  Placement = pos=(0,0,0) rot=(1,0,0;1.5708rad)
  Profile = -> Sketch001
  ReferenceAxis = -> Sketch001 [N_Axis]
  Suppressed = false
  Type = 1
FEATURE [PartDesign::Fillet] Fillet
  Base = -> Pocket [Edge24,Edge4,Edge23,Edge3]
  BaseFeature = -> Pocket
  Placement = pos=(0,0,0) rot=(1,0,0;1.5708rad)
  Radius = 9.99
  SupportTransform = false
  Suppressed = false
  UseAllEdges = false
FEATURE [PartDesign::Chamfer] Chamfer
  Angle = 45
  Base = -> Fillet [Edge12,Edge13,Edge14,Edge15,Edge16,Edge17]
  BaseFeature = -> Fillet
  ChamferType = 0
  FlipDirection = false
  Placement = pos=(0,0,0) rot=(1,0,0;1.5708rad)
  Size = 2
  Size2 = 1
  SupportTransform = false
  Suppressed = false
  UseAllEdges = false
FEATURE [PartDesign::Body] Body
  AllowCompound = false
  Group = -> [Sketch,Pad,Sketch001,Pocket,Fillet,Chamfer]
  Origin = -> Origin
  Tip = -> Chamfer
FEATURE [TechDraw::DrawSVGTemplate] Template001
  EditableTexts = AuthorName=Matthias Mosimann; CheckDate=N/A; CreationDate=11/04/2026; DrawingNumber=1.0; FC-Title=Verstellmechanik; SheetNumber=1 / 1; SupervisorName=N/A; Weight=WEIGHT; scale=1 : 3
  Height = 297
  Orientation = 1
  Template = C:/Program Files/FreeCAD 1.0/data/Mod/TechDraw/Templates/A3_Landscape_TD.svg
  Width = 420
FEATURE [TechDraw::DrawProjGroupItem] View  label="Front"
  CoarseView = false
  Direction = (0,-1,0)
  Focus = 100
  HardHidden = false
  IsoCount = 0
  IsoHidden = false
  IsoVisible = false
  LockPosition = true
  Perspective = false
  Rotation = 0
  RotationVector = (1,0,0)
  Scale = 0.333333
  ScaleType = 2
  ScrubCount = 1
  SeamHidden = false
  SeamVisible = true
  SmoothHidden = false
  SmoothVisible = true
  Source = -> [Body]
  Type = 0
  X = 0
  XDirection = (1,0,5e-16)
  Y = 0
FEATURE [TechDraw::DrawProjGroupItem] ProjItem001  label="Left"
  CoarseView = false
  Direction = (-1,-1e-16,-5e-16)
  Focus = 100
  HardHidden = true
  IsoCount = 0
  IsoHidden = false
  IsoVisible = false
  LockPosition = true
  Perspective = false
  Rotation = 0
  RotationVector = (1,0,0)
  Scale = 0.333333
  ScaleType = 0
  ScrubCount = 1
  SeamHidden = false
  SeamVisible = true
  SmoothHidden = false
  SmoothVisible = true
  Source = -> [Body]
  Type = 1
  X = 108.481
  XDirection = (1e-16,-1,0)
  Y = 0
FEATURE [TechDraw::DrawProjGroupItem] View001
  CoarseView = false
  Direction = (-0.57735,0.57735,0.57735)
  Focus = 100
  HardHidden = false
  IsoCount = 0
  IsoHidden = false
  IsoVisible = false
  LockPosition = true
  Perspective = false
  Rotation = 0
  RotationVector = (1,0,0)
  Scale = 0.5
  ScaleType = 2
  ScrubCount = 1
  SeamHidden = false
  SeamVisible = true
  SmoothHidden = false
  SmoothVisible = true
  Source = -> [Body]
  Type = 0
  X = 311.468
  XDirection = (5.7735e-07,0.707107,-0.707107)
  Y = 226.51
FEATURE [TechDraw::DrawProjGroupItem] View002
  CoarseView = false
  Direction = (-0.57735,-0.57735,-0.57735)
  Focus = 100
  HardHidden = false
  IsoCount = 0
  IsoHidden = false
  IsoVisible = false
  LockPosition = true
  Perspective = false
  Rotation = 0
  RotationVector = (1,0,0)
  Scale = 0.5
  ScaleType = 2
  ScrubCount = 1
  SeamHidden = false
  SeamVisible = true
  SmoothHidden = false
  SmoothVisible = true
  Source = -> [Body]
  Type = 0
  X = 311.468
  XDirection = (0,-0.707107,0.707107)
  Y = 135.86
FEATURE [TechDraw::DrawProjGroupItem] ProjItem  label="Top"
  CoarseView = false
  Direction = (-5e-16,0,1)
  Focus = 100
  HardHidden = false
  IsoCount = 0
  IsoHidden = false
  IsoVisible = false
  LockPosition = true
  Perspective = false
  Rotation = 0
  RotationVector = (1,0,0)
  Scale = 0.333333
  ScaleType = 0
  ScrubCount = 1
  SeamHidden = false
  SeamVisible = true
  SmoothHidden = false
  SmoothVisible = true
  Source = -> [Body]
  Type = 4
  X = 0
  XDirection = (1,0,5e-16)
  Y = -107.5
FEATURE [TechDraw::DrawProjGroup] ProjGroup
  Anchor = -> View
  AutoDistribute = true
  LockPosition = false
  ProjectionType = 0
  Rotation = 0
  Scale = 0.333333
  ScaleType = 2
  Source = -> [Body]
  Views = -> [View,ProjItem001,ProjItem]
  X = 30.1017
  Y = 226.055
  spacingX = 25
  spacingY = 25
FEATURE [TechDraw::DrawViewDimension] Dimension001
  AngleOverride = false
  Arbitrary = false
  ArbitraryTolerances = false
  BoxCorners = (2) [(-3.33333,-81.6667,0),(3.33333,81.6667,0)]
  EqualTolerance = true
  ExtensionAngle = 0
  FormatSpec = %.2w
  FormatSpecOverTolerance = %+.2w
  FormatSpecUnderTolerance = %+.2w
  Inverted = false
  LineAngle = 0
  LockPosition = false
  MeasureType = 1
  OverTolerance = 0
  References2D = -> [ProjItem]
  Rotation = 0
  ScaleType = 0
  TheoreticalExact = false
  Type = 2
  UnderTolerance = 0
  X = 19.7807
  Y = 61.3333
FEATURE [TechDraw::DrawViewDimension] Dimension
  AngleOverride = false
  Arbitrary = false
  ArbitraryTolerances = false
  BoxCorners = (2) [(-3.33333,-81.6667,0),(3.33333,81.6667,0)]
  EqualTolerance = true
  ExtensionAngle = 0
  FormatSpec = %.2w
  FormatSpecOverTolerance = %+.2w
  FormatSpecUnderTolerance = %+.2w
  Inverted = false
  LineAngle = 0
  LockPosition = false
  MeasureType = 1
  OverTolerance = 0
  References2D = -> [ProjItem]
  Rotation = 0
  ScaleType = 0
  TheoreticalExact = false
  Type = 2
  UnderTolerance = 0
  X = 19.7807
  Y = 30.6667
FEATURE [TechDraw::DrawViewDimension] Dimension002
  AngleOverride = false
  Arbitrary = false
  ArbitraryTolerances = false
  BoxCorners = (2) [(-3.33333,-81.6667,0),(3.33333,81.6667,0)]
  EqualTolerance = true
  ExtensionAngle = 0
  FormatSpec = %.2w
  FormatSpecOverTolerance = %+.2w
  FormatSpecUnderTolerance = %+.2w
  Inverted = false
  LineAngle = 0
  LockPosition = false
  MeasureType = 1
  OverTolerance = 0
  References2D = -> [ProjItem]
  Rotation = 0
  ScaleType = 0
  TheoreticalExact = false
  Type = 2
  UnderTolerance = 0
  X = 19.7807
  Y = 0
FEATURE [TechDraw::DrawViewDimension] Dimension003
  AngleOverride = false
  Arbitrary = false
  ArbitraryTolerances = false
  BoxCorners = (2) [(-3.33333,-81.6667,0),(3.33333,81.6667,0)]
  EqualTolerance = true
  ExtensionAngle = 0
  FormatSpec = %.2w
  FormatSpecOverTolerance = %+.2w
  FormatSpecUnderTolerance = %+.2w
  Inverted = false
  LineAngle = 0
  LockPosition = false
  MeasureType = 1
  OverTolerance = 0
  References2D = -> [ProjItem]
  Rotation = 0
  ScaleType = 0
  TheoreticalExact = false
  Type = 2
  UnderTolerance = 0
  X = 19.7807
  Y = -30.6667
FEATURE [TechDraw::DrawViewDimension] Dimension004
  AngleOverride = false
  Arbitrary = false
  ArbitraryTolerances = false
  BoxCorners = (2) [(-3.33333,-81.6667,0),(3.33333,81.6667,0)]
  EqualTolerance = true
  ExtensionAngle = 0
  FormatSpec = %.2w
  FormatSpecOverTolerance = %+.2w
  FormatSpecUnderTolerance = %+.2w
  Inverted = false
  LineAngle = 0
  LockPosition = false
  MeasureType = 1
  OverTolerance = 0
  References2D = -> [ProjItem]
  Rotation = 0
  ScaleType = 0
  TheoreticalExact = false
  Type = 2
  UnderTolerance = 0
  X = 19.7807
  Y = -61.3333
FEATURE [TechDraw::DrawViewDimension] Dimension005
  AngleOverride = false
  Arbitrary = false
  ArbitraryTolerances = false
  BoxCorners = (2) [(-81.6667,-0.833333,-1e-07),(81.6667,0.833333,1e-07)]
  EqualTolerance = true
  ExtensionAngle = 0
  FormatSpec = %.2w
  FormatSpecOverTolerance = %+.2w
  FormatSpecUnderTolerance = %+.2w
  Inverted = false
  LineAngle = 0
  LockPosition = false
  MeasureType = 1
  OverTolerance = 0
  References2D = -> [ProjItem001]
  Rotation = 0
  ScaleType = 0
  TheoreticalExact = false
  Type = 0
  UnderTolerance = 0
  X = 0
  Y = 25.316
FEATURE [TechDraw::DrawViewDimension] Dimension006
  AngleOverride = false
  Arbitrary = false
  ArbitraryTolerances = false
  BoxCorners = (2) [(-3.33333,-0.833333,-1e-07),(3.33333,0.833333,1e-07)]
  EqualTolerance = true
  ExtensionAngle = 0
  FormatSpec = %.2w
  FormatSpecOverTolerance = %+.2w
  FormatSpecUnderTolerance = %+.2w
  Inverted = false
  LineAngle = 0
  LockPosition = false
  MeasureType = 1
  OverTolerance = 0
  References2D = -> [View]
  Rotation = 0
  ScaleType = 0
  TheoreticalExact = false
  Type = 0
  UnderTolerance = 0
  X = 11.0143
  Y = 5.04996
FEATURE [TechDraw::DrawViewDimension] Dimension007
  AngleOverride = false
  Arbitrary = false
  ArbitraryTolerances = false
  BoxCorners = (2) [(-3.33333,-0.833333,-1e-07),(3.33333,0.833333,1e-07)]
  EqualTolerance = true
  ExtensionAngle = 0
  FormatSpec = %.2w
  FormatSpecOverTolerance = %+.2w
  FormatSpecUnderTolerance = %+.2w
  Inverted = false
  LineAngle = 0
  LockPosition = false
  MeasureType = 1
  OverTolerance = 0
  References2D = -> [View]
  Rotation = 0
  ScaleType = 0
  TheoreticalExact = false
  Type = 0
  UnderTolerance = 0
  X = 0
  Y = 12.3217
FEATURE [TechDraw::DrawViewDimension] Dimension008
  AngleOverride = false
  Arbitrary = false
  ArbitraryTolerances = false
  BoxCorners = (2) [(-3.33333,-81.6667,0),(3.33333,81.6667,0)]
  EqualTolerance = true
  ExtensionAngle = 0
  FormatSpec = ⌀%.2w
  FormatSpecOverTolerance = %+.2w
  FormatSpecUnderTolerance = %+.2w
  Inverted = false
  LineAngle = 0
  LockPosition = false
  MeasureType = 1
  OverTolerance = 0
  References2D = -> [ProjItem]
  Rotation = 0
  ScaleType = 0
  TheoreticalExact = false
  Type = 5
  UnderTolerance = 0
  X = 13.438
  Y = 88.727
FEATURE [TechDraw::DrawViewBalloon] Balloon
  BubbleShape = 0
  EndType = 0
  EndTypeScale = 1
  KinkLength = 5
  LockPosition = false
  OriginX = -4.15
  OriginY = 230
  Rotation = 0
  ScaleType = 0
  ShapeScale = 1
  SourceView = -> ProjItem
  Text = 1
  TextWrapLen = -1
  X = -41.6343
  Y = 259.425
FEATURE [TechDraw::DrawViewDimension] Dimension009
  AngleOverride = false
  Arbitrary = false
  ArbitraryTolerances = false
  BoxCorners = (2) [(-3.33333,-81.6667,0),(3.33333,81.6667,0)]
  EqualTolerance = true
  ExtensionAngle = 0
  FormatSpec = ⌀%.2w
  FormatSpecOverTolerance = %+.2w
  FormatSpecUnderTolerance = %+.2w
  Inverted = false
  LineAngle = 0
  LockPosition = false
  MeasureType = 1
  OverTolerance = 0
  References2D = -> [ProjItem]
  Rotation = 0
  ScaleType = 0
  TheoreticalExact = false
  Type = 5
  UnderTolerance = 0
  X = 12.9248
  Y = 57.6148
FEATURE [TechDraw::DrawViewBalloon] Balloon001
  BubbleShape = 0
  EndType = 0
  EndTypeScale = 1
  KinkLength = 5
  LockPosition = false
  OriginX = -4.15
  OriginY = 138
  Rotation = 0
  ScaleType = 0
  ShapeScale = 1
  SourceView = -> ProjItem
  Text = 2
  TextWrapLen = -1
  X = -41.3681
  Y = 171.843
FEATURE [TechDraw::DrawViewDimension] Dimension010
  AngleOverride = false
  Arbitrary = false
  ArbitraryTolerances = false
  BoxCorners = (2) [(-3.33333,-81.6667,0),(3.33333,81.6667,0)]
  EqualTolerance = true
  ExtensionAngle = 0
  FormatSpec = %.2w
  FormatSpecOverTolerance = %+.2w
  FormatSpecUnderTolerance = %+.2w
  Inverted = false
  LineAngle = 0
  LockPosition = false
  MeasureType = 1
  OverTolerance = 0
  References2D = -> [ProjItem]
  Rotation = 0
  ScaleType = 0
  TheoreticalExact = false
  Type = 0
  UnderTolerance = 0
  X = -12.7793
  Y = -77.9341
FEATURE [TechDraw::DrawViewAnnotation] Annotation005
  Font = osifont
  LineSpace = 80
  LockPosition = false
  MaxWidth = 120
  Rotation = 0
  ScaleType = 0
  Text = Teil wird aus standard Stahlprofil hergestellt 20mm x 5mm. Alle Angaben in mm. 3D Ansichten können von der angegebenen Skalierungsgrösse abweichen.
  TextSize = 3
  TextStyle = 1
  X = 138.582
  Y = 178.803
FEATURE [TechDraw::DrawViewAnnotation] Annotation
  Font = osifont
  LineSpace = 80
  LockPosition = false
  MaxWidth = 120
  Rotation = 0
  ScaleType = 0
  Text = (1) Durchgangsloch M4 fein (kann auch grösser sein M5/M6). Achtung, muss aber dann ingesamt angepasst werden. | (2) Senkung ist auf M4 angepasst.
  TextSize = 3
  TextStyle = 0
  X = 138.582
  Y = 143.805
FEATURE [TechDraw::DrawPage] Page001
  KeepUpdated = true
  NextBalloonIndex = 4
  ProjectionType = 0
  Template = -> Template001
  Views = -> [ProjGroup,View001,View002,Dimension001,Dimension,Dimension002,Dimension003,Dimension004,Dimension005,Dimension006,Dimension007,Dimension008,Balloon,Dimension009,Balloon001,Dimension010,Annotation005,Annotation]
---- part 10_assembly_lamella_no_knob.FCStd = doc fcstd_8ccdfd1235f6 ----
FCSTD DOCUMENT  (FreeCAD 1.0R39319 (Git))
Label: 10_assembly_lamella_no_knob
License: All rights reserved
LicenseURL: http://en.wikipedia.org/wiki/All_rights_reserved
objects: App::FeaturePython×11, App::Link×3, TechDraw::DrawViewBalloon×2, Assembly::ViewGroup×1, TechDraw::DrawSVGTemplate×1, TechDraw::DrawProjGroupItem×1, TechDraw::DrawPage×1, Assembly::JointGroup×1, Assembly::AssemblyObject×1
EXTERNAL_REF file=12_lamella_sheet_no_knob.FCStd obj=Body
EXTERNAL_REF file=17_lamella_back.FCStd obj=Body
EXTERNAL_REF file=18_lamella_l_holder.FCStd obj=Body

FEATURE [App::Link] Body
  LinkedObject = -> <external 12_lamella_sheet_no_knob.FCStd>#Body
FEATURE [App::FeaturePython] GroundedJoint  # Assembly grounded joint (typed FeaturePython)
  ObjectToGround = -> Body
FEATURE [App::Link] Body001
  LinkPlacement = pos=(-9.4e-15,-6e-15,4.5) rot=(0,0,1;0rad)
  LinkedObject = -> <external 17_lamella_back.FCStd>#Body
  Placement = pos=(-9.4e-15,-6e-15,4.5) rot=(0,0,1;0rad)
FEATURE [App::FeaturePython] Joint  label="Distance"  # Assembly joint (typed FeaturePython)
  Activated = true
  AngleMax = 0
  AngleMin = 0
  Detach1 = false
  Detach2 = false
  Distance = 0
  Distance2 = 0
  EnableAngleMax = false
  EnableAngleMin = false
  EnableLengthMax = false
  EnableLengthMin = false
  JointType = 5 (Distance)
  LengthMax = 0
  LengthMin = 0
  Placement1 = pos=(0,-1e-16,-3) rot=(0,0,1;0rad)
  Placement2 = pos=(1e-15,3e-16,1.5) rot=(0,0,1;0rad)
  Reference1 = -> Assembly [Body001.Face3,Body001.Vertex8]
  Reference2 = -> Assembly [Body.Face6,Body.Vertex6]
FEATURE [App::FeaturePython] Joint001  label="Distance001"  # Assembly joint (typed FeaturePython)
  Activated = true
  AngleMax = 0
  AngleMin = 0
  Detach1 = false
  Detach2 = false
  Distance = 0
  Distance2 = 0
  EnableAngleMax = false
  EnableAngleMin = false
  EnableLengthMax = false
  EnableLengthMin = false
  JointType = 5 (Distance)
  LengthMax = 0
  LengthMin = 0
  Placement1 = pos=(208,-4e-16,0) rot=(-0.57735,-0.57735,0.57735;2.0944rad)
  Placement2 = pos=(208,-9e-16,0) rot=(-0.57735,-0.57735,0.57735;2.0944rad)
  Reference1 = -> Assembly [Body001.Face7,Body001.Vertex8]
  Reference2 = -> Assembly [Body.Face3,Body.Face3]
FEATURE [App::FeaturePython] Joint002  label="Distance002"  # Assembly joint (typed FeaturePython)
  Activated = true
  AngleMax = 0
  AngleMin = 0
  Detach1 = false
  Detach2 = false
  Distance = -42.5
  Distance2 = 0
  EnableAngleMax = false
  EnableAngleMin = false
  EnableLengthMax = false
  EnableLengthMin = false
  JointType = 5 (Distance)
  LengthMax = 0
  LengthMin = 0
  Placement1 = pos=(0,-7.5,0) rot=(-1,0,0;1.5708rad)
  Placement2 = pos=(1e-15,-50,0) rot=(-1,0,0;1.5708rad)
  Reference1 = -> Assembly [Body001.Face5,Body001.Vertex8]
  Reference2 = -> Assembly [Body.Face2,Body.Vertex5]
FEATURE [App::Link] Body002
  LinkPlacement = pos=(-4,77.5,1.5) rot=(0,-1,0;1.5708rad)
  LinkedObject = -> <external 18_lamella_l_holder.FCStd>#Body
  Placement = pos=(-4,77.5,1.5) rot=(0,-1,0;1.5708rad)
FEATURE [App::FeaturePython] Joint005  label="Distance005"  # Assembly joint (typed FeaturePython)
  Activated = true
  AngleMax = 0
  AngleMin = 0
  Detach1 = false
  Detach2 = false
  Distance = -204
  Distance2 = 0
  EnableAngleMax = false
  EnableAngleMin = false
  EnableLengthMax = false
  EnableLengthMin = false
  JointType = 5 (Distance)
  LengthMax = 0
  LengthMin = 0
  Placement1 = pos=(12.2633,-28.0749,1.29e-14) rot=(0,-1,0;3.14159rad)
  Placement2 = pos=(-208,9e-16,0) rot=(0.57735,-0.57735,0.57735;4.18879rad)
  Reference1 = -> Assembly [Body002.Face1,Body002.Face1]
  Reference2 = -> Assembly [Body.Face1,Body.Face1]
FEATURE [App::FeaturePython] Move  # WARN: FeaturePython — macro-defined, semantics opaque (R4)
  MoveType = 0
  MovementTransform = pos=(0,81,0) rot=(0,-1.00436,0;0rad)
  References = -> Assembly [Body002.]
FEATURE [App::FeaturePython] Move001  # WARN: FeaturePython — macro-defined, semantics opaque (R4)
  MoveType = 0
  MovementTransform = pos=(-1e-05,0,66) rot=(0,0,1;0rad)
  References = -> Assembly [Body002.]
FEATURE [App::FeaturePython] Move002  # WARN: FeaturePython — macro-defined, semantics opaque (R4)
  MoveType = 0
  MovementTransform = pos=(0,-1e-05,113) rot=(0,0,1;0rad)
  References = -> Assembly [Body001.]
FEATURE [App::FeaturePython] Exploded_View  # WARN: FeaturePython — macro-defined, semantics opaque (R4)
  Group = -> [Move,Move001,Move002]
FEATURE [Assembly::ViewGroup] Exploded_Views
  Group = -> [Exploded_View]
FEATURE [TechDraw::DrawSVGTemplate] Template
  EditableTexts = AuthorName=AUTHOR NAME; CheckDate=CHECK DATE; CreationDate=11/04/2026; DrawingNumber=NUMBER; FC-Title=10_assembly_lamella_no_knob; SheetNumber=1 / 1; Subtitle=SUBTITLE; SupervisorName=SUPERVISOR NAME; Weight=WEIGHT; scale=1 : 1
  Height = 297
  Orientation = 1
  Template = C:/Program Files/FreeCAD 1.0/data/Mod/TechDraw/Templates/A3_Landscape_TD.svg
  Width = 420
FEATURE [TechDraw::DrawProjGroupItem] View
  CoarseView = false
  Direction = (0.57735,-0.57735,0.57735)
  Focus = 100
  HardHidden = false
  IsoCount = 0
  IsoHidden = false
  IsoVisible = false
  LockPosition = false
  Perspective = false
  Rotation = 0
  RotationVector = (1,0,0)
  Scale = 0.5
  ScaleType = 2
  ScrubCount = 1
  SeamHidden = false
  SeamVisible = true
  SmoothHidden = false
  SmoothVisible = true
  Source = -> [Exploded_View]
  Type = 0
  X = 133.185
  XDirection = (0.707107,0.707107,0)
  Y = 187.394
FEATURE [TechDraw::DrawViewBalloon] Balloon
  BubbleShape = 0
  EndType = 0
  EndTypeScale = 1
  KinkLength = 5
  LockPosition = false
  OriginX = 89.0955
  OriginY = 41.131
  Rotation = 0
  ScaleType = 0
  ShapeScale = 1
  SourceView = -> View
  Text = 1
  TextWrapLen = -1
  X = 157.793
  Y = 78.8802
FEATURE [TechDraw::DrawViewBalloon] Balloon001
  BubbleShape = 0
  EndType = 0
  EndTypeScale = 1
  KinkLength = 5
  LockPosition = false
  OriginX = -3.21137e-06
  OriginY = 5.61341
  Rotation = 0
  ScaleType = 0
  ShapeScale = 1
  SourceView = -> View
  Text = 2
  TextWrapLen = -1
  X = -123.182
  Y = -68.6141
FEATURE [TechDraw::DrawPage] Page
  KeepUpdated = true
  NextBalloonIndex = 3
  ProjectionType = 0
  Template = -> Template
  Views = -> [View,Balloon,Balloon001]
FEATURE [App::FeaturePython] Joint006  label="Distance006"  # Assembly joint (typed FeaturePython)
  Activated = true
  AngleMax = 0
  AngleMin = 0
  Detach1 = false
  Detach2 = false
  Distance = 0
  Distance2 = 0
  EnableAngleMax = false
  EnableAngleMin = false
  EnableLengthMax = false
  EnableLengthMin = false
  JointType = 5 (Distance)
  LengthMax = 0
  LengthMin = 0
  Placement1 = pos=(0,-39.066,-5.94913) rot=(0,-1,0;4.71239rad)
  Placement2 = pos=(1e-15,3e-16,1.5) rot=(0,0,1;0rad)
  Reference1 = -> Assembly [Body002.Face4,Body002.Face4]
  Reference2 = -> Assembly [Body.Face6,Body.Face6]
FEATURE [App::FeaturePython] Joint007  label="Distance007"  # Assembly joint (typed FeaturePython)
  Activated = true
  AngleMax = 0
  AngleMin = 0
  Detach1 = false
  Detach2 = false
  Distance = 0
  Distance2 = 0
  EnableAngleMax = false
  EnableAngleMin = false
  EnableLengthMax = false
  EnableLengthMin = false
  JointType = 5 (Distance)
  LengthMax = 0
  LengthMin = 0
  Placement1 = pos=(1.5,-70,-6.5) rot=(-0.57735,-0.57735,-0.57735;2.0944rad)
  Placement2 = pos=(3e-16,7.5,0) rot=(0,-0.707107,0.707107;3.14159rad)
  Reference1 = -> Assembly [Body002.Face6,Body002.Face6]
  Reference2 = -> Assembly [Body001.Face2,Body001.Face2]
FEATURE [Assembly::JointGroup] Joints
  Group = -> [GroundedJoint,Joint,Joint001,Joint002,Joint005,Joint006,Joint007]
FEATURE [Assembly::AssemblyObject] Assembly
  Group = -> [Joints,Body,GroundedJoint,Body001,Joint,Joint001,Joint002,Body002,Joint005,Exploded_Views,Exploded_View,Move,Move001,Move002,Joint006,Joint007]
  Origin = -> Origin
  Type = Assembly
---- part 11_assembly_lamella_knob.FCStd = doc fcstd_95b1bbc4cee9 ----
FCSTD DOCUMENT  (FreeCAD 1.0R39319 (Git))
Label: 11_assembly_lamella_knob
License: All rights reserved
LicenseURL: http://en.wikipedia.org/wiki/All_rights_reserved
objects: App::FeaturePython×14, App::Link×4, TechDraw::DrawProjGroupItem×4, TechDraw::DrawViewDimension×3, TechDraw::DrawViewBalloon×3, TechDraw::DrawViewAnnotation×2, Assembly::ViewGroup×1, TechDraw::DrawSVGTemplate×1, Assembly::JointGroup×1, Assembly::AssemblyObject×1, TechDraw::DrawProjGroup×1, TechDraw::DrawPage×1
note: 5 computed .brp shape members not serialized (recipe doc carries the construction recipe); baked Part::Feature solids carry a one-line shape summary decoded from their .brp
EXTERNAL_REF file=13_lamella_sheet_knob.FCStd obj=Body
EXTERNAL_REF file=17_lamella_back.FCStd obj=Body
EXTERNAL_REF file=18_lamella_l_holder.FCStd obj=Body
EXTERNAL_REF file=19_knob.FCStd obj=Body

FEATURE [App::Link] Body
  LinkedObject = -> <external 13_lamella_sheet_knob.FCStd>#Body
FEATURE [App::FeaturePython] GroundedJoint  # Assembly grounded joint (typed FeaturePython)
  ObjectToGround = -> Body
FEATURE [App::Link] Body001
  LinkPlacement = pos=(-1.1e-14,-5.1e-15,4.5) rot=(1,0,0;3.14159rad)
  LinkedObject = -> <external 17_lamella_back.FCStd>#Body
  Placement = pos=(-1.1e-14,-5.1e-15,4.5) rot=(1,0,0;3.14159rad)
FEATURE [App::Link] Body002
  LinkPlacement = pos=(-5,77.5,1.5) rot=(0,-1,0;1.5708rad)
  LinkedObject = -> <external 18_lamella_l_holder.FCStd>#Body
  Placement = pos=(-5,77.5,1.5) rot=(0,-1,0;1.5708rad)
FEATURE [App::Link] Body003
  LinkPlacement = pos=(8,-30,-1.5) rot=(0.57735,0.57735,-0.57735;2.0944rad)
  LinkedObject = -> <external 19_knob.FCStd>#Body
  Placement = pos=(8,-30,-1.5) rot=(0.57735,0.57735,-0.57735;2.0944rad)
FEATURE [App::FeaturePython] Joint  label="Fixed"  # Assembly joint (typed FeaturePython)
  Activated = true
  AngleMax = 0
  AngleMin = 0
  Detach1 = false
  Detach2 = false
  Distance = 0
  Distance2 = 0
  EnableAngleMax = false
  EnableAngleMin = false
  EnableLengthMax = false
  EnableLengthMin = false
  JointType = 0 (Fixed)
  LengthMax = 0
  LengthMin = 0
  Placement1 = pos=(8,-30,-1.5) rot=(0,0,1;0rad)
  Placement2 = pos=(0,0,0) rot=(0.57735,0.57735,0.57735;2.0944rad)
  Reference1 = -> Assembly [Body.Edge17,Body.Edge17]
  Reference2 = -> Assembly [Body003.Edge2,Body003.Edge2]
FEATURE [App::FeaturePython] Joint001  label="Distance"  # Assembly joint (typed FeaturePython)
  Activated = true
  AngleMax = 0
  AngleMin = 0
  Detach1 = false
  Detach2 = false
  Distance = 0
  Distance2 = 0
  EnableAngleMax = false
  EnableAngleMin = false
  EnableLengthMax = false
  EnableLengthMin = false
  JointType = 5 (Distance)
  LengthMax = 0
  LengthMin = 0
  Placement1 = pos=(5e-16,0,3) rot=(0,0,1;0rad)
  Placement2 = pos=(-0.0232159,0.0870598,1.5) rot=(0,0,1;0rad)
  Reference1 = -> Assembly [Body001.Face4,Body001.Face4]
  Reference2 = -> Assembly [Body.Face1,Body.Vertex3]
FEATURE [App::FeaturePython] Joint002  label="Distance001"  # Assembly joint (typed FeaturePython)
  Activated = true
  AngleMax = 0
  AngleMin = 0
  Detach1 = false
  Detach2 = false
  Distance = -42.5
  Distance2 = 0
  EnableAngleMax = false
  EnableAngleMin = false
  EnableLengthMax = false
  EnableLengthMin = false
  JointType = 5 (Distance)
  LengthMax = 0
  LengthMin = 0
  Placement1 = pos=(5e-16,7.5,0) rot=(0,0.707107,-0.707107;3.14159rad)
  Placement2 = pos=(1e-15,-50,0) rot=(-1,0,0;1.5708rad)
  Reference1 = -> Assembly [Body001.Face2,Body001.Vertex6]
  Reference2 = -> Assembly [Body.Face5,Body.Face5]
FEATURE [App::FeaturePython] Joint003  label="Distance002"  # Assembly joint (typed FeaturePython)
  Activated = true
  AngleMax = 0
  AngleMin = 0
  Detach1 = false
  Detach2 = false
  Distance = 0
  Distance2 = 0
  EnableAngleMax = false
  EnableAngleMin = false
  EnableLengthMax = false
  EnableLengthMin = false
  JointType = 5 (Distance)
  LengthMax = 0
  LengthMin = 0
  Placement1 = pos=(208,-4e-16,0) rot=(0.57735,0.57735,-0.57735;4.18879rad)
  Placement2 = pos=(208,-9e-16,0) rot=(-0.57735,-0.57735,0.57735;2.0944rad)
  Reference1 = -> Assembly [Body001.Face7,Body001.Vertex11]
  Reference2 = -> Assembly [Body.Face6,Body.Face6]
FEATURE [App::FeaturePython] Joint006  label="Distance005"  # Assembly joint (typed FeaturePython)
  Activated = true
  AngleMax = 0
  AngleMin = 0
  Detach1 = false
  Detach2 = false
  Distance = 203
  Distance2 = 0
  EnableAngleMax = false
  EnableAngleMin = false
  EnableLengthMax = false
  EnableLengthMin = false
  JointType = 5 (Distance)
  LengthMax = 0
  LengthMin = 0
  Placement1 = pos=(-208,9e-16,0) rot=(0.57735,-0.57735,0.57735;4.18879rad)
  Placement2 = pos=(12.2633,-28.0749,1.24e-14) rot=(0,-1,0;3.14159rad)
  Reference1 = -> Assembly [Body.Face3,Body.Face3]
  Reference2 = -> Assembly [Body002.Face1,Body002.Face1]
FEATURE [App::FeaturePython] Move  # WARN: FeaturePython — macro-defined, semantics opaque (R4)
  MoveType = 0
  MovementTransform = pos=(0,86,0) rot=(0,-1.00436,0;0rad)
  References = -> Assembly [Body002.]
FEATURE [App::FeaturePython] Move001  # WARN: FeaturePython — macro-defined, semantics opaque (R4)
  MoveType = 0
  MovementTransform = pos=(-1e-05,0,43) rot=(0,0,1;0rad)
  References = -> Assembly [Body002.]
FEATURE [App::FeaturePython] Move002  # WARN: FeaturePython — macro-defined, semantics opaque (R4)
  MoveType = 0
  MovementTransform = pos=(0,-1e-05,74) rot=(1.00436,0,0;0rad)
  References = -> Assembly [Body001.]
FEATURE [App::FeaturePython] Move003  # WARN: FeaturePython — macro-defined, semantics opaque (R4)
  MoveType = 0
  MovementTransform = pos=(-1e-05,0,-46) rot=(0,0,1;0rad)
  References = -> Assembly [Body003.]
FEATURE [App::FeaturePython] Move004  # WARN: FeaturePython — macro-defined, semantics opaque (R4)
  MoveType = 0
  MovementTransform = pos=(0,-90,0) rot=(0.579865,0.579865,-0.579865;0rad)
  References = -> Assembly [Body003.]
FEATURE [App::FeaturePython] Exploded_View  # WARN: FeaturePython — macro-defined, semantics opaque (R4)
  Group = -> [Move,Move001,Move002,Move003,Move004]
FEATURE [Assembly::ViewGroup] Exploded_Views
  Group = -> [Exploded_View]
FEATURE [TechDraw::DrawSVGTemplate] Template
  EditableTexts = AuthorName=Matthias Mosimann; CheckDate=N/a; CreationDate=15/04/2026; DrawingNumber=1.0; FC-Title=Baugruppe Lamelle; SheetNumber=1 / 1; SupervisorName=N/A; Weight=N/A; scale=1 : 2
  Height = 297
  Orientation = 1
  Template = C:/Program Files/FreeCAD 1.0/data/Mod/TechDraw/Templates/A3_Landscape_TD.svg
  Width = 420
FEATURE [TechDraw::DrawViewAnnotation] Annotation005
  Font = osifont
  LineSpace = 80
  LockPosition = false
  MaxWidth = 120
  Rotation = 0
  Scale = 0.5
  ScaleType = 1
  Text = Baugruppe mit Lamellen Rücken und Lamellenhalter. | Alle Teile werden geschweisst.  | 3D Ansichten können von der angegebenen Skalierungsgrösse abweichen. | Alle Angaben in mm.
  TextSize = 3
  TextStyle = 1
  X = 338.543
  Y = 195.021
FEATURE [TechDraw::DrawViewAnnotation] Annotation
  Font = osifont
  LineSpace = 80
  LockPosition = false
  MaxWidth = 120
  Rotation = 0
  Scale = 0.75
  ScaleType = 1
  Text = (1) Bauteil Lamellenhalter | (2) Bauteil Lamellenrücken | (3) Griff (Achtung nur bei einer Lamelle) - wird durch M6 Schraube motniert.
  TextSize = 3
  TextStyle = 0
  X = 338.543
  Y = 152.527
FEATURE [App::FeaturePython] Joint007  label="Distance006"  # Assembly joint (typed FeaturePython)
  Activated = true
  AngleMax = 0
  AngleMin = 0
  Detach1 = false
  Detach2 = false
  Distance = 0
  Distance2 = 0
  EnableAngleMax = false
  EnableAngleMin = false
  EnableLengthMax = false
  EnableLengthMin = false
  JointType = 5 (Distance)
  LengthMax = 0
  LengthMin = 0
  Placement1 = pos=(-2e-16,-39.066,-5.94913) rot=(0,-1,0;4.71239rad)
  Placement2 = pos=(-0.0232159,0.0870598,1.5) rot=(0,0,1;0rad)
  Reference1 = -> Assembly [Body002.Face4,Body002.Face4]
  Reference2 = -> Assembly [Body.Face1,Body.Face1]
FEATURE [App::FeaturePython] Joint008  label="Distance007"  # Assembly joint (typed FeaturePython)
  Activated = true
  AngleMax = 0
  AngleMin = 0
  Detach1 = false
  Detach2 = false
  Distance = 0
  Distance2 = 0
  EnableAngleMax = false
  EnableAngleMin = false
  EnableLengthMax = false
  EnableLengthMin = false
  JointType = 5 (Distance)
  LengthMax = 0
  LengthMin = 0
  Placement1 = pos=(1.5,-70,-6.5) rot=(-0.57735,-0.57735,-0.57735;2.0944rad)
  Placement2 = pos=(5e-16,-7.5,0) rot=(-1,0,0;1.5708rad)
  Reference1 = -> Assembly [Body002.Face6,Body002.Face6]
  Reference2 = -> Assembly [Body001.Face5,Body001.Face5]
FEATURE [Assembly::JointGroup] Joints
  Group = -> [GroundedJoint,Joint,Joint001,Joint002,Joint003,Joint006,Joint007,Joint008]
FEATURE [Assembly::AssemblyObject] Assembly
  Group = -> [Joints,Body,GroundedJoint,Body001,Body002,Body003,Joint,Joint001,Joint002,Joint003,Joint006,Exploded_Views,Exploded_View,Move,Move001,Move002,Move003,Move004,Joint007,Joint008]
  Origin = -> Origin
  Type = Assembly
FEATURE [TechDraw::DrawProjGroupItem] View  label="Front"
  CoarseView = false
  Direction = (0,-1,0)
  Focus = 100
  HardHidden = false
  IsoCount = 0
  IsoHidden = false
  IsoVisible = false
  LockPosition = true
  Perspective = false
  Rotation = 0
  RotationVector = (1,0,0)
  Scale = 0.5
  ScaleType = 2
  ScrubCount = 1
  SeamHidden = false
  SeamVisible = true
  SmoothHidden = false
  SmoothVisible = true
  Source = -> [Assembly]
  Type = 0
  X = 0
  XDirection = (1,0,0)
  Y = 0
FEATURE [TechDraw::DrawProjGroupItem] ProjItem  label="Left"
  CoarseView = false
  Direction = (-1,-1e-16,0)
  Focus = 100
  HardHidden = false
  IsoCount = 0
  IsoHidden = false
  IsoVisible = false
  LockPosition = true
  Perspective = false
  Rotation = 0
  RotationVector = (1,0,0)
  Scale = 0.5
  ScaleType = 2
  ScrubCount = 1
  SeamHidden = false
  SeamVisible = true
  SmoothHidden = false
  SmoothVisible = true
  Source = -> [Assembly]
  Type = 1
  X = 213.717
  XDirection = (1e-16,-1,0)
  Y = 0
FEATURE [TechDraw::DrawProjGroupItem] ProjItem001  label="Top"
  CoarseView = false
  Direction = (0,0,1)
  Focus = 100
  HardHidden = false
  IsoCount = 0
  IsoHidden = false
  IsoVisible = false
  LockPosition = true
  Perspective = false
  Rotation = 0
  RotationVector = (1,0,0)
  Scale = 0.5
  ScaleType = 2
  ScrubCount = 1
  SeamHidden = false
  SeamVisible = true
  SmoothHidden = false
  SmoothVisible = true
  Source = -> [Assembly]
  Type = 4
  X = 0
  XDirection = (1,0,0)
  Y = -85.4363
FEATURE [TechDraw::DrawViewDimension] Dimension
  AngleOverride = false
  Arbitrary = false
  ArbitraryTolerances = false
  BoxCorners = (2) [(-107.5,-31.875,-1e-07),(107.5,31.875,1e-07)]
  EqualTolerance = true
  ExtensionAngle = 0
  FormatSpec = %.2w
  FormatSpecOverTolerance = %+.2w
  FormatSpecUnderTolerance = %+.2w
  Inverted = false
  LineAngle = 0
  LockPosition = false
  MeasureType = 1
  OverTolerance = 0
  References2D = -> [ProjItem001]
  Rotation = 0
  ScaleType = 0
  TheoreticalExact = false
  Type = 0
  UnderTolerance = 0
  X = -44.4252
  Y = 31.9811
FEATURE [TechDraw::DrawViewDimension] Dimension001
  AngleOverride = false
  Arbitrary = false
  ArbitraryTolerances = false
  BoxCorners = (2) [(-107.5,-31.875,-1e-07),(107.5,31.875,1e-07)]
  EqualTolerance = true
  ExtensionAngle = 0
  FormatSpec = %.2w
  FormatSpecOverTolerance = %+.2w
  FormatSpecUnderTolerance = %+.2w
  Inverted = false
  LineAngle = 0
  LockPosition = false
  MeasureType = 1
  OverTolerance = 0
  References2D = -> [ProjItem001]
  Rotation = 0
  ScaleType = 0
  TheoreticalExact = false
  Type = 0
  UnderTolerance = 0
  X = -116.032
  Y = -21.25
FEATURE [TechDraw::DrawViewDimension] Dimension002
  AngleOverride = false
  Arbitrary = false
  ArbitraryTolerances = false
  BoxCorners = (2) [(-107.5,-31.875,-1e-07),(107.5,31.875,1e-07)]
  EqualTolerance = true
  ExtensionAngle = 0
  FormatSpec = %.2w
  FormatSpecOverTolerance = %+.2w
  FormatSpecUnderTolerance = %+.2w
  Inverted = false
  LineAngle = 0
  LockPosition = false
  MeasureType = 1
  OverTolerance = 0
  References2D = -> [ProjItem001]
  Rotation = 0
  ScaleType = 0
  TheoreticalExact = false
  Type = 2
  UnderTolerance = 0
  X = -130.943
  Y = 7.5
FEATURE [TechDraw::DrawProjGroupItem] ProjItem002  label="FrontTopLeft"
  CoarseView = false
  Direction = (-0.57735,-0.57735,0.57735)
  Focus = 100
  HardHidden = false
  IsoCount = 0
  IsoHidden = false
  IsoVisible = false
  LockPosition = true
  Perspective = false
  Rotation = 0
  RotationVector = (1,0,0)
  ScaleType = 0
  ScrubCount = 1
  SeamHidden = false
  SeamVisible = true
  SmoothHidden = false
  SmoothVisible = true
  Source = -> [Assembly]
  Type = 6
  X = -17.0248
  XDirection = (0.707107,-0.707107,0)
  Y = -185.884
FEATURE [TechDraw::DrawProjGroup] ProjGroup
  Anchor = -> View
  AutoDistribute = true
  LockPosition = false
  ProjectionType = 0
  Rotation = 0
  Scale = 0.5
  ScaleType = 2
  Source = -> [Assembly]
  Views = -> [View,ProjItem,ProjItem001,ProjItem002]
  X = 140.983
  Y = 254.027
  spacingX = 15
  spacingY = 15
FEATURE [TechDraw::DrawViewBalloon] Balloon
  BubbleShape = 0
  EndType = 0
  EndTypeScale = 1
  KinkLength = 5
  LockPosition = false
  OriginX = -24.5135
  OriginY = 25.2431
  Rotation = 0
  ScaleType = 0
  ShapeScale = 1
  SourceView = -> ProjItem002
  Text = 1
  TextWrapLen = -1
  X = 15.4865
  Y = 65.2431
FEATURE [TechDraw::DrawViewBalloon] Balloon001
  BubbleShape = 0
  EndType = 0
  EndTypeScale = 1
  KinkLength = 5
  LockPosition = false
  OriginX = 133.74
  OriginY = 91.3191
  Rotation = 0
  ScaleType = 0
  ShapeScale = 1
  SourceView = -> ProjItem002
  Text = 2
  TextWrapLen = -1
  X = 163.332
  Y = 13.3522
FEATURE [TechDraw::DrawViewBalloon] Balloon002
  BubbleShape = 0
  EndType = 0
  EndTypeScale = 1
  KinkLength = 5
  LockPosition = false
  OriginX = 36.3046
  OriginY = -40.7841
  Rotation = 0
  ScaleType = 0
  ShapeScale = 1
  SourceView = -> ProjItem002
  Text = 3
  TextWrapLen = -1
  X = 90.877
  Y = -61.8493
FEATURE [TechDraw::DrawPage] Page
  KeepUpdated = true
  NextBalloonIndex = 4
  ProjectionType = 0
  Template = -> Template
  Views = -> [ProjGroup,Dimension,Dimension001,Dimension002,Annotation005,Balloon,Balloon001,Annotation,Balloon002]
